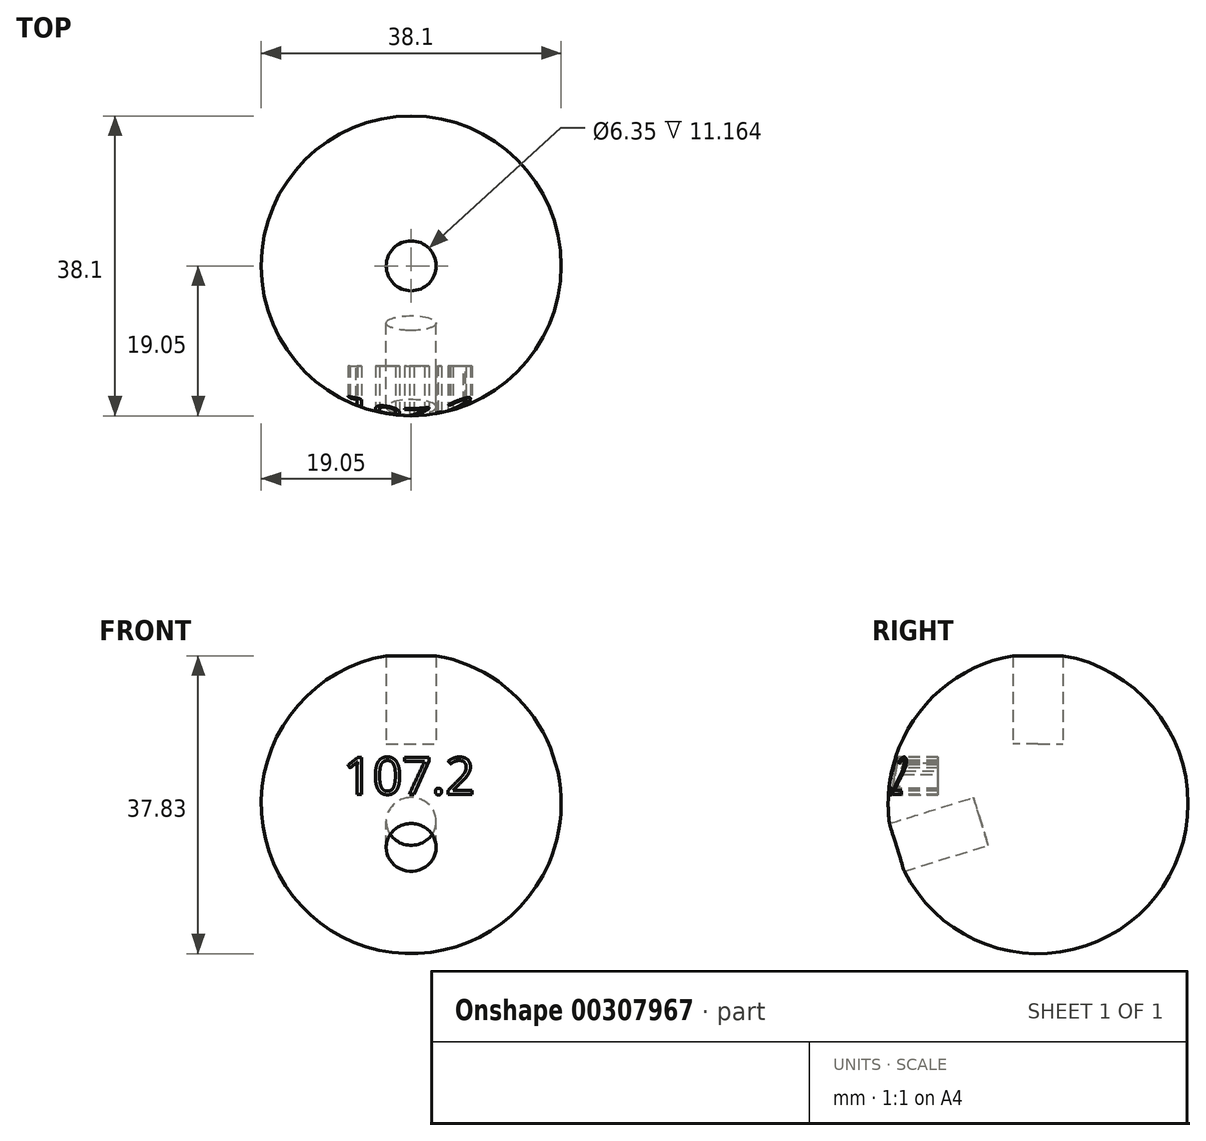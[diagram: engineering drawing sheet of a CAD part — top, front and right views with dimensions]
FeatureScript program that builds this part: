
annotation { "Feature Type Name" : "Feature", "Feature Type Description" : "" }
export const myFeature = defineFeature(function(context is Context, id is Id, definition is map)
    precondition{}
    {
        {
            var Q0;
            Q0=qCreatedBy(makeId("Front.planeOp"),FACE);
            var sketch = newSketch(context, id + "F0", { "sketchPlane" : qUnion([Q0])});
            skCircle(sketch, "E0", {"center": v(0, 0) * mm, "radius": 19.05 * mm});
            skSolve(sketch);
        }
        {
            var Q0;
            Q0=qCreatedBy(makeId("Top.planeOp"),FACE);
            var sketch = newSketch(context, id + "F1", { "sketchPlane" : qUnion([Q0])});
            skArc(sketch, "E1", {"start": v(0, 19.05) * mm, "mid": v(-19.05, 0) * mm, "end": v(0, -19.05) * mm});
            skLineSegment(sketch, "E2", {"start": v(0, -19.05) * mm, "end": v(0, 19.05) * mm});
            skSolve(sketch);
        }
        {
            var Q0;
            Q0=makeQuery(id+"F1.imprint","IMPRINT",FACE,{"disambiguationData":[TD([[makeQuery(id+"F1.imprint","IMPRINT",EDGE,{"derivedFrom":sQuery(id+"F1.wireOp",EDGE,"E1")}),1.0]])]});
            var Q1;
            Q1=sQuery(id+"F0.wireOp",EDGE,"E0");
            revolve(context, id + "F2", {"entities" : qUnion([Q0]), "axis" : qUnion([Q1]), "revolveType" : RevolveType.FULL});
        }
        {
            var Q0;
            Q0=qCreatedBy(makeId("Top.planeOp"),FACE);
            var sketch = newSketch(context, id + "F3", { "sketchPlane" : qUnion([Q0])});
            skLineSegment(sketch, "E3", {"start": v(0, 0) * mm, "end": v(0, 73.19) * mm, "construction": true});
            skLineSegment(sketch, "E4", {"start": v(0, 0) * mm, "end": v(77.24, 0) * mm, "construction": true});
            skSolve(sketch);
        }
        {
            var Q0;
            Q0=qCreatedBy(makeId("Top.planeOp"),FACE);
            cPlane(context, id + "F4", {"entities" : qUnion([Q0]), "cplaneType" : CPlaneType.OFFSET, "offset" : 7.62 * mm, "width" : 152.4 * mm, "height" : 152.4 * mm});
        }
        {
            var Q0;
            Q0=qCreatedBy(id+"F4.planeOp",FACE);
            var sketch = newSketch(context, id + "F5", { "sketchPlane" : qUnion([Q0])});
            skCircle(sketch, "E5", {"center": v(0, 0) * mm, "radius": 3.18 * mm});
            skSolve(sketch);
        }
        {
            var Q0;
            Q0 = qSketchRegion(id + "F5", true);
            extrude(context, id + "F6", {"entities" : qUnion([Q0]), "depth" : 50.8 * mm});
        }
        {
            var Q0;
            Q0=makeQuery(id+"F6.opExtrude","SWEPT_BODY",BODY,{"disambiguationData":[OSD([sQuery(id+"F5.wireOp",EDGE,"E5")])]});
            var Q1;
            Q1=sQuery(id+"F3.wireOp",EDGE,"E4");
            var Q2;
            Q2=sQuery(id+"F3.wireOp",EDGE,"E4");
            transform(context, id + "F7", {"entities" : qUnion([Q0]), "transformType" : TransformType.ROTATION, "transformAxis" : qUnion([Q2]), "angle" : 107.2 * degree, "makeCopy" : true});
        }
        {
            var Q0;
            Q0=makeQuery(id+"F6.opExtrude","SWEPT_BODY",BODY,{"disambiguationData":[OSD([sQuery(id+"F5.wireOp",EDGE,"E5")])]});
            var Q1;
            Q1=makeQuery(id+"F7.opPattern","COPY",BODY,{"derivedFrom":makeQuery(id+"F6.opExtrude","SWEPT_BODY",BODY,{"disambiguationData":[OSD([sQuery(id+"F5.wireOp",EDGE,"E5")])]}),"instanceName":"1"});
            var Q2;
            Q2=makeQuery(id+"F2.opRevolve","SWEPT_BODY",BODY,{"disambiguationData":[OSD([sQuery(id+"F1.wireOp",EDGE,"E1"),sQuery(id+"F1.wireOp",EDGE,"E2")])]});
            booleanBodies(context, id + "F8", {"operationType" : BooleanOperationType.SUBTRACTION, "tools" : qUnion([Q0, Q1]), "targets" : qUnion([Q2])});
        }
        {
            var Q0;
            Q0=qCreatedBy(makeId("Front.planeOp"),FACE);
            cPlane(context, id + "F9", {"entities" : qUnion([Q0]), "cplaneType" : CPlaneType.OFFSET, "offset" : 19.05 * mm, "width" : 152.4 * mm, "height" : 152.4 * mm});
        }
        {
            var Q0;
            Q0=qCreatedBy(id+"F9.planeOp",FACE);
            var sketch = newSketch(context, id + "F10", { "sketchPlane" : qUnion([Q0])});
            skText(sketch, "E6", { "text": "107.2", "fontName": "OpenSans-Regular.ttf"});
            const initialGuessF10  = {"E6": [-0.00862, 0.0012, 1, 0, 0.00471]};
            skSetInitialGuess(sketch, initialGuessF10);
            skSolve(sketch);
        }
        {
            var Q0;
            Q0 = qSketchRegion(id + "F10", true);
            extrude(context, id + "F11", {"entities" : qUnion([Q0]), "operationType" : NewBodyOperationType.REMOVE, "oppositeDirection" : true, "depth" : 6.35 * mm});
        }
    });
